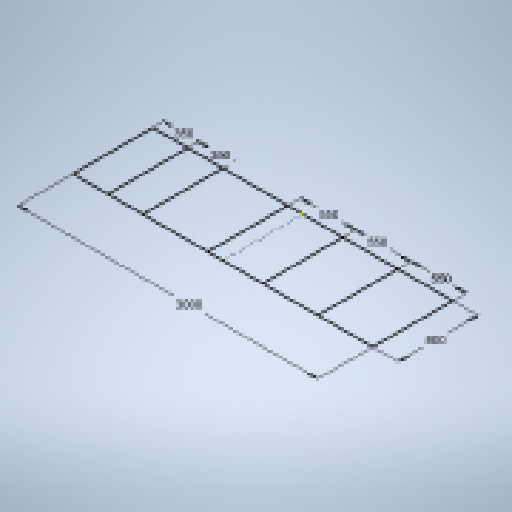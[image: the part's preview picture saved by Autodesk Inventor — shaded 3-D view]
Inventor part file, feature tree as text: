
AUTODESK INVENTOR PART (.ipt)
format: ipt  version: 2025 (Build 290162010, 162A)  size: 138,752 bytes
history: native  units: mm
features: sketch x1
ambient origin geometry x8: Origin, YZ Plane, XZ Plane, XY Plane, X Axis, Y Axis, Z Axis, Center Point
feature tree (1):
  sketch  "Sketch1"  dims[d0=3000.0mm d1=800.0mm d2=1500.0mm d14=600.0mm d16=550.0mm d17=550.0mm d18=350.0mm d20=550.0mm d21=350.0mm]
